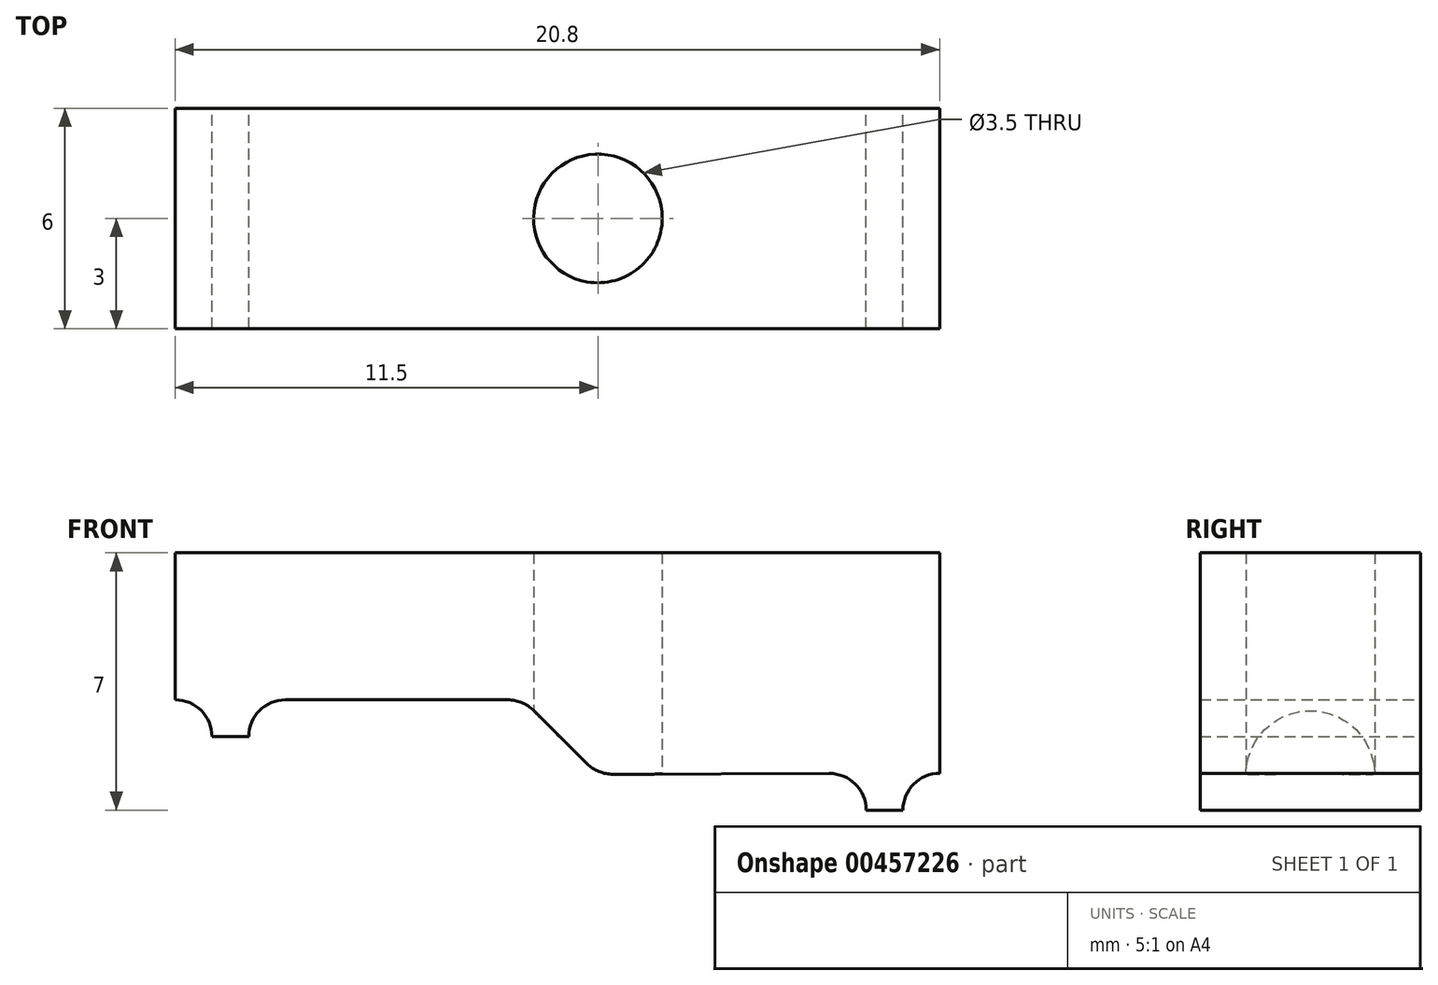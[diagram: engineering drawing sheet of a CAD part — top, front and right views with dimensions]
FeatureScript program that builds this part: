
annotation { "Feature Type Name" : "Feature", "Feature Type Description" : "" }
export const myFeature = defineFeature(function(context is Context, id is Id, definition is map)
    precondition{}
    {
        {
            var Q0;
            Q0=qCreatedBy(makeId("Front.planeOp"),FACE);
            var sketch = newSketch(context, id + "F0", { "sketchPlane" : qUnion([Q0])});
            skLineSegment(sketch, "E0", {"start": v(0, 0) * mm, "end": v(20.8, 0) * mm});
            skLineSegment(sketch, "E1", {"start": v(20.8, 0) * mm, "end": v(20.8, -6) * mm});
            skLineSegment(sketch, "E2", {"start": v(20.8, -6) * mm, "end": v(19.8, -6) * mm});
            skLineSegment(sketch, "E3", {"start": v(19.8, -7) * mm, "end": v(19.8, -6) * mm});
            skLineSegment(sketch, "E4", {"start": v(11.5, -6.03) * mm, "end": v(9.46, -4) * mm});
            skLineSegment(sketch, "E5", {"start": v(9.46, -4) * mm, "end": v(2, -4) * mm});
            skLineSegment(sketch, "E6", {"start": v(2, -4) * mm, "end": v(2, -5) * mm});
            skLineSegment(sketch, "E7", {"start": v(2, -5) * mm, "end": v(1, -5) * mm});
            skLineSegment(sketch, "E8", {"start": v(1, -5) * mm, "end": v(1, -4) * mm});
            skLineSegment(sketch, "E9", {"start": v(1, -4) * mm, "end": v(0, -4) * mm});
            skLineSegment(sketch, "E10", {"start": v(0, -4) * mm, "end": v(0, 0) * mm});
            skLineSegment(sketch, "E11", {"start": v(19.8, -7) * mm, "end": v(18.8, -7) * mm});
            skLineSegment(sketch, "E12", {"start": v(18.8, -7) * mm, "end": v(18.8, -6) * mm});
            skLineSegment(sketch, "E13", {"start": v(11.5, -6.03) * mm, "end": v(18.8, -6) * mm});
            skSolve(sketch);
        }
        {
            var Q0;
            Q0=makeQuery(id+"F0.imprint","IMPRINT",FACE,{"disambiguationData":[TD([[makeQuery(id+"F0.imprint","IMPRINT",EDGE,{"derivedFrom":sQuery(id+"F0.wireOp",EDGE,"E0")}),-1.0]])]});
            extrude(context, id + "F1", {"entities" : qUnion([Q0]), "depth" : 6 * mm});
        }
        {
            var Q0;
            Q0=makeQuery(id+"F1.opExtrude","SWEPT_FACE",FACE,{"disambiguationData":[OSD([sQuery(id+"F0.wireOp",EDGE,"E5")])]});
            var sketch = newSketch(context, id + "F2", { "sketchPlane" : qUnion([Q0])});
            skCircle(sketch, "E14", {"center": v(11.5, 3) * mm, "radius": 1.75 * mm});
            skSolve(sketch);
        }
        {
            var Q0;
            Q0 = qSketchRegion(id + "F2", true);
            extrude(context, id + "F3", {"entities" : qUnion([Q0]), "operationType" : NewBodyOperationType.REMOVE, "endBound" : BoundingType.THROUGH_ALL, "oppositeDirection" : true, "depth" : 25 * mm, "hasSecondDirection" : true, "secondDirectionBound" : SecondDirectionBoundingType.THROUGH_ALL, "secondDirectionOppositeDirection" : false, "secondDirectionDepth" : 25 * mm});
        }
        {
            var Q0;
            Q0=makeQuery(id+"F1.opExtrude","SWEPT_EDGE",EDGE,{"disambiguationData":[OSD([sQuery(id+"F0.wireOp",EDGE,"E2"),sQuery(id+"F0.wireOp",EDGE,"E3")])]});
            var Q1;
            Q1=makeQuery(id+"F1.opExtrude","SWEPT_EDGE",EDGE,{"disambiguationData":[OSD([sQuery(id+"F0.wireOp",EDGE,"E4"),sQuery(id+"F0.wireOp",EDGE,"E13")])]});
            var Q2;
            {var subQ0=sQuery(id+"F0.wireOp",EDGE,"E5");var subQ1=sQuery(id+"F0.wireOp",EDGE,"E4");Q2=makeQuery(id+"F3.boolean.opBoolean","SPLIT",EDGE,{"disambiguationData":[TD([makeQuery(id+"F1.opExtrude","CAP_FACE",FACE,{"disambiguationData":[OSD([sQuery(id+"F0.wireOp",EDGE,"E0"),sQuery(id+"F0.wireOp",EDGE,"E1"),sQuery(id+"F0.wireOp",EDGE,"E2"),sQuery(id+"F0.wireOp",EDGE,"E3"),subQ1,subQ0,sQuery(id+"F0.wireOp",EDGE,"E6"),sQuery(id+"F0.wireOp",EDGE,"E7"),sQuery(id+"F0.wireOp",EDGE,"E8"),sQuery(id+"F0.wireOp",EDGE,"E9"),sQuery(id+"F0.wireOp",EDGE,"E10"),sQuery(id+"F0.wireOp",EDGE,"E11"),sQuery(id+"F0.wireOp",EDGE,"E12"),sQuery(id+"F0.wireOp",EDGE,"E13")])],"isStart":false})])],"derivedFrom":makeQuery(id+"F1.opExtrude","SWEPT_EDGE",EDGE,{"disambiguationData":[OSD([subQ1,subQ0])]})});}
            var Q3;
            Q3=makeQuery(id+"F1.opExtrude","SWEPT_EDGE",EDGE,{"disambiguationData":[OSD([sQuery(id+"F0.wireOp",EDGE,"E5"),sQuery(id+"F0.wireOp",EDGE,"E6")])]});
            var Q4;
            Q4=makeQuery(id+"F1.opExtrude","SWEPT_EDGE",EDGE,{"disambiguationData":[OSD([sQuery(id+"F0.wireOp",EDGE,"E8"),sQuery(id+"F0.wireOp",EDGE,"E9")])]});
            var Q5;
            Q5=makeQuery(id+"F1.opExtrude","SWEPT_EDGE",EDGE,{"disambiguationData":[OSD([sQuery(id+"F0.wireOp",EDGE,"E12"),sQuery(id+"F0.wireOp",EDGE,"E13")])]});
            fillet(context, id + "F4", {"entities" : qUnion([Q0, Q1, Q2, Q3, Q4, Q5]), "radius" : 1 * mm, "tangentPropagation" : true, "allowEdgeOverflow" : false});
        }
    });
